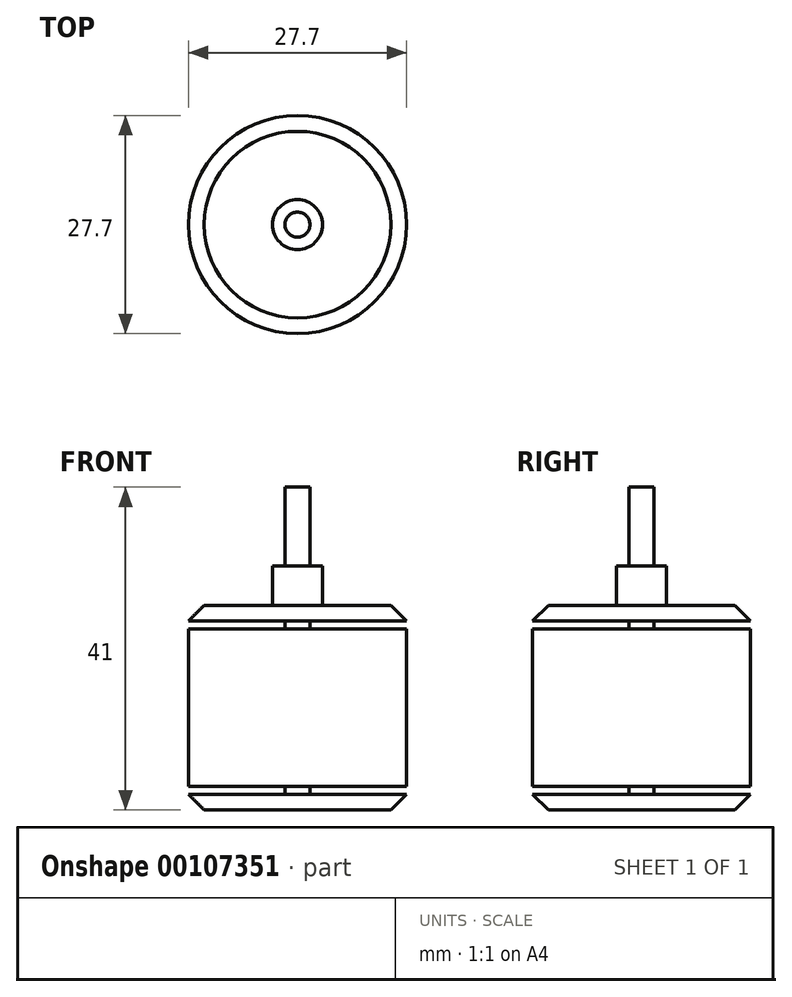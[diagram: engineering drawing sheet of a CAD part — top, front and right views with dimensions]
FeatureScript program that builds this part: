
annotation { "Feature Type Name" : "Feature", "Feature Type Description" : "" }
export const myFeature = defineFeature(function(context is Context, id is Id, definition is map)
    precondition{}
    {
        {
            var Q0;
            Q0=qCreatedBy(makeId("Front.planeOp"),FACE);
            var sketch = newSketch(context, id + "F0", { "sketchPlane" : qUnion([Q0])});
            skLineSegment(sketch, "E0", {"start": v(0, 0) * mm, "end": v(-11.85, 0) * mm});
            skLineSegment(sketch, "E1", {"start": v(-11.85, 0) * mm, "end": v(-13.85, 2) * mm});
            skLineSegment(sketch, "E2", {"start": v(-13.85, 2) * mm, "end": v(-1.59, 2) * mm});
            skLineSegment(sketch, "E3", {"start": v(0, 2) * mm, "end": v(0, 0) * mm});
            skLineSegment(sketch, "E4.bottom", {"start": v(-1.59, 3) * mm, "end": v(-13.85, 3) * mm});
            skLineSegment(sketch, "E4.top", {"start": v(-1.59, 23) * mm, "end": v(-13.85, 23) * mm});
            skLineSegment(sketch, "E4.left", {"start": v(0, 3) * mm, "end": v(0, 23) * mm});
            skLineSegment(sketch, "E4.right", {"start": v(-13.85, 3) * mm, "end": v(-13.85, 23) * mm});
            skLineSegment(sketch, "E5", {"start": v(-1.59, 24) * mm, "end": v(-13.85, 24) * mm});
            skLineSegment(sketch, "E6", {"start": v(-13.85, 24) * mm, "end": v(-11.85, 26) * mm});
            skLineSegment(sketch, "E7", {"start": v(-11.85, 26) * mm, "end": v(-3.18, 26) * mm});
            skLineSegment(sketch, "E8", {"start": v(0, 26) * mm, "end": v(0, 24) * mm});
            skLineSegment(sketch, "E9.top", {"start": v(-1.59, 31) * mm, "end": v(-3.18, 31) * mm});
            skLineSegment(sketch, "E9.left", {"start": v(0, 26) * mm, "end": v(0, 31) * mm});
            skLineSegment(sketch, "E9.right", {"start": v(-3.17, 26) * mm, "end": v(-3.18, 31) * mm});
            skLineSegment(sketch, "E10.top", {"start": v(0, 41) * mm, "end": v(-1.59, 41) * mm});
            skLineSegment(sketch, "E10.left", {"start": v(0, 31) * mm, "end": v(0, 41) * mm});
            skLineSegment(sketch, "E10.right", {"start": v(-1.59, 31) * mm, "end": v(-1.59, 41) * mm});
            skLineSegment(sketch, "E11", {"start": v(0, 3) * mm, "end": v(0, 2) * mm});
            skLineSegment(sketch, "E12", {"start": v(0, 23) * mm, "end": v(0, 24) * mm});
            skLineSegment(sketch, "E13", {"start": v(-1.59, 24) * mm, "end": v(-1.59, 23) * mm});
            skLineSegment(sketch, "E14", {"start": v(-1.59, 2) * mm, "end": v(-1.59, 3) * mm});
            skSolve(sketch);
        }
        {
            var Q0;
            Q0=qSketchRegion(id+"F0",true);
            var Q1;
            Q1=sQuery(id+"F0.wireOp",EDGE,"E4.left");
            revolve(context, id + "F1", {"entities" : qUnion([Q0]), "axis" : qUnion([Q1]), "revolveType" : RevolveType.FULL});
        }
    });
